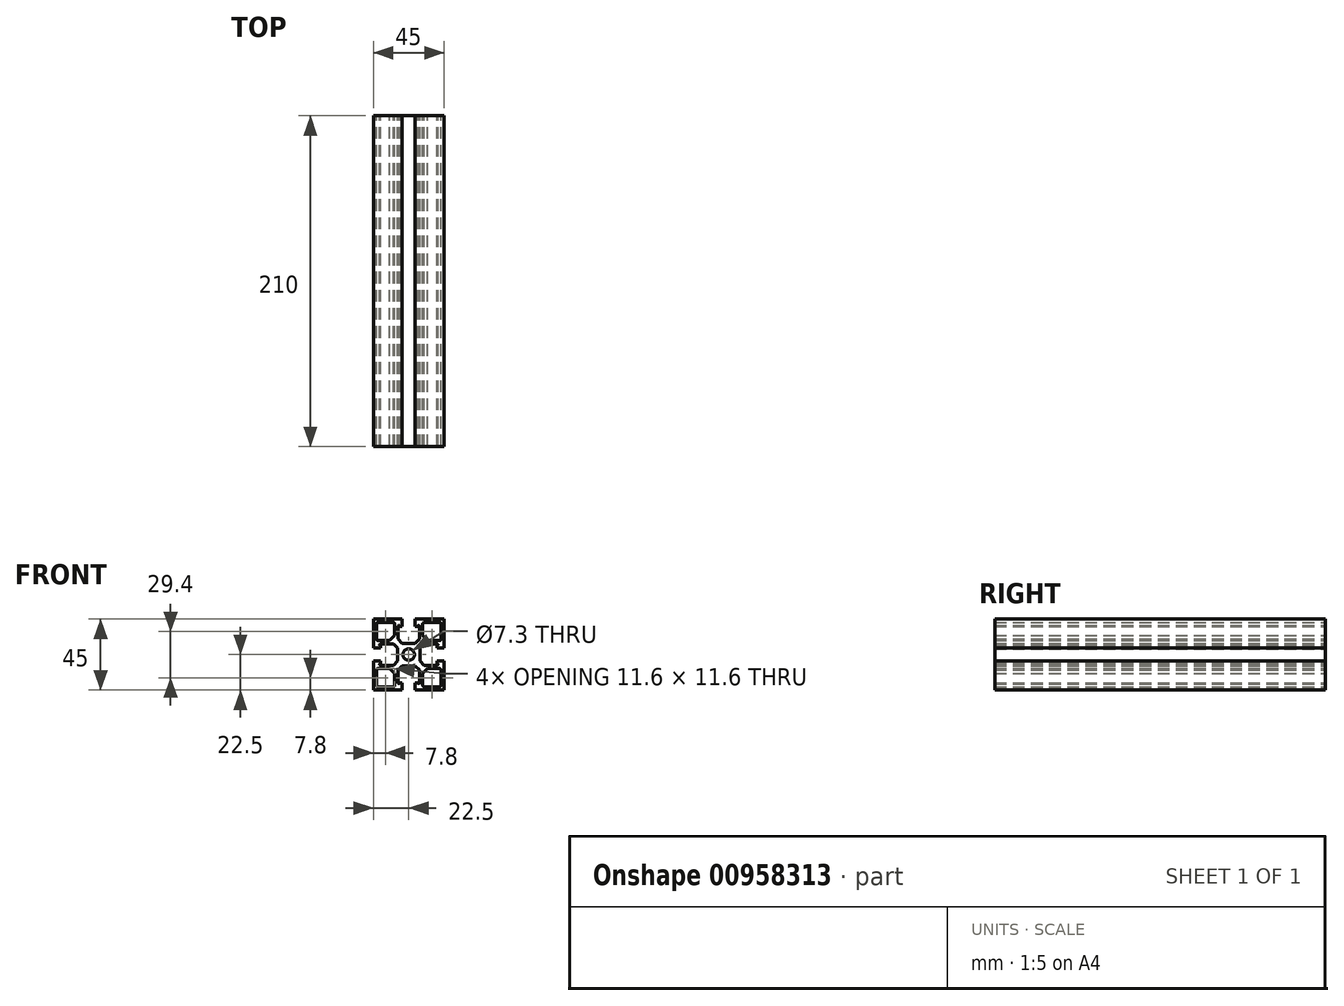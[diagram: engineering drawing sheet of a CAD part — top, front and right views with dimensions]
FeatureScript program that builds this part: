
annotation { "Feature Type Name" : "Feature", "Feature Type Description" : "" }
export const myFeature = defineFeature(function(context is Context, id is Id, definition is map)
    precondition{}
    {
        {
            var Q0;
            Q0=qCreatedBy(makeId("Front.planeOp"),FACE);
            var sketch = newSketch(context, id + "F0", { "sketchPlane" : qUnion([Q0])});
            skLineSegment(sketch, "E0", {"start": v(-22.5, 22.5) * mm, "end": v(-4.15, 22.5) * mm});
            skLineSegment(sketch, "E1", {"start": v(-4.15, 22.5) * mm, "end": v(-4.15, 18) * mm});
            skLineSegment(sketch, "E2", {"start": v(-4.15, 18) * mm, "end": v(-5.75, 18) * mm});
            skArc(sketch, "E3", {"start": v(-5.75, 18) * mm, "mid": v(-6.25, 18.5) * mm, "end": v(-6.75, 18) * mm});
            skLineSegment(sketch, "E4", {"start": v(-6.75, 18) * mm, "end": v(-6.75, 9.8) * mm});
            skLineSegment(sketch, "E5", {"start": v(-6.75, 9.8) * mm, "end": v(-4.15, 7.2) * mm});
            skLineSegment(sketch, "E6", {"start": v(-4.15, 7.2) * mm, "end": v(4.15, 7.2) * mm});
            skLineSegment(sketch, "E7", {"start": v(4.15, 7.2) * mm, "end": v(6.75, 9.8) * mm});
            skLineSegment(sketch, "E8", {"start": v(6.75, 9.8) * mm, "end": v(6.75, 18) * mm});
            skArc(sketch, "E9", {"start": v(6.75, 18) * mm, "mid": v(6.25, 18.5) * mm, "end": v(5.75, 18) * mm});
            skLineSegment(sketch, "E10", {"start": v(5.75, 18) * mm, "end": v(4.15, 18) * mm});
            skLineSegment(sketch, "E11", {"start": v(4.15, 18) * mm, "end": v(4.15, 22.5) * mm});
            skLineSegment(sketch, "E12", {"start": v(4.15, 22.5) * mm, "end": v(22.5, 22.5) * mm});
            skLineSegment(sketch, "E13", {"start": v(22.5, 22.5) * mm, "end": v(22.5, 4.15) * mm});
            skLineSegment(sketch, "E14", {"start": v(22.5, 4.15) * mm, "end": v(18, 4.15) * mm});
            skLineSegment(sketch, "E15", {"start": v(18, 4.15) * mm, "end": v(18, 5.75) * mm});
            skArc(sketch, "E16", {"start": v(18, 5.75) * mm, "mid": v(18.5, 6.25) * mm, "end": v(18, 6.75) * mm});
            skLineSegment(sketch, "E17", {"start": v(18, 6.75) * mm, "end": v(9.8, 6.75) * mm});
            skLineSegment(sketch, "E18", {"start": v(9.8, 6.75) * mm, "end": v(7.2, 4.15) * mm});
            skLineSegment(sketch, "E19", {"start": v(7.2, 4.15) * mm, "end": v(7.2, -4.15) * mm});
            skLineSegment(sketch, "E20", {"start": v(7.2, -4.15) * mm, "end": v(9.8, -6.75) * mm});
            skLineSegment(sketch, "E21", {"start": v(9.8, -6.75) * mm, "end": v(18, -6.75) * mm});
            skArc(sketch, "E22", {"start": v(18, -6.75) * mm, "mid": v(18.5, -6.25) * mm, "end": v(18, -5.75) * mm});
            skLineSegment(sketch, "E23", {"start": v(18, -5.75) * mm, "end": v(18, -4.15) * mm});
            skLineSegment(sketch, "E24", {"start": v(18, -4.15) * mm, "end": v(22.5, -4.15) * mm});
            skLineSegment(sketch, "E25", {"start": v(22.5, -4.15) * mm, "end": v(22.5, -22.5) * mm});
            skLineSegment(sketch, "E26", {"start": v(22.5, -22.5) * mm, "end": v(4.15, -22.5) * mm});
            skLineSegment(sketch, "E27", {"start": v(4.15, -22.5) * mm, "end": v(4.15, -18) * mm});
            skLineSegment(sketch, "E28", {"start": v(4.15, -18) * mm, "end": v(5.75, -18) * mm});
            skArc(sketch, "E29", {"start": v(5.75, -18) * mm, "mid": v(6.25, -18.5) * mm, "end": v(6.75, -18) * mm});
            skLineSegment(sketch, "E30", {"start": v(6.75, -18) * mm, "end": v(6.75, -9.8) * mm});
            skLineSegment(sketch, "E31", {"start": v(6.75, -9.8) * mm, "end": v(4.15, -7.2) * mm});
            skLineSegment(sketch, "E32", {"start": v(4.15, -7.2) * mm, "end": v(-4.15, -7.2) * mm});
            skLineSegment(sketch, "E33", {"start": v(-4.15, -7.2) * mm, "end": v(-6.75, -9.8) * mm});
            skLineSegment(sketch, "E34", {"start": v(-6.75, -9.8) * mm, "end": v(-6.75, -18) * mm});
            skArc(sketch, "E35", {"start": v(-6.75, -18) * mm, "mid": v(-6.25, -18.5) * mm, "end": v(-5.75, -18) * mm});
            skLineSegment(sketch, "E36", {"start": v(-5.75, -18) * mm, "end": v(-4.15, -18) * mm});
            skLineSegment(sketch, "E37", {"start": v(-4.15, -18) * mm, "end": v(-4.15, -22.5) * mm});
            skLineSegment(sketch, "E38", {"start": v(-4.15, -22.5) * mm, "end": v(-22.5, -22.5) * mm});
            skLineSegment(sketch, "E39", {"start": v(-22.5, -22.5) * mm, "end": v(-22.5, -4.15) * mm});
            skLineSegment(sketch, "E40", {"start": v(-22.5, -4.15) * mm, "end": v(-18, -4.15) * mm});
            skLineSegment(sketch, "E41", {"start": v(-18, -4.15) * mm, "end": v(-18, -5.75) * mm});
            skArc(sketch, "E42", {"start": v(-18, -5.75) * mm, "mid": v(-18.5, -6.25) * mm, "end": v(-18, -6.75) * mm});
            skLineSegment(sketch, "E43", {"start": v(-18, -6.75) * mm, "end": v(-9.8, -6.75) * mm});
            skLineSegment(sketch, "E44", {"start": v(-9.8, -6.75) * mm, "end": v(-7.2, -4.15) * mm});
            skLineSegment(sketch, "E45", {"start": v(-7.2, -4.15) * mm, "end": v(-7.2, 4.15) * mm});
            skLineSegment(sketch, "E46", {"start": v(-7.2, 4.15) * mm, "end": v(-9.8, 6.75) * mm});
            skLineSegment(sketch, "E47", {"start": v(-9.8, 6.75) * mm, "end": v(-18, 6.75) * mm});
            skArc(sketch, "E48", {"start": v(-18, 6.75) * mm, "mid": v(-18.5, 6.25) * mm, "end": v(-18, 5.75) * mm});
            skLineSegment(sketch, "E49", {"start": v(-18, 5.75) * mm, "end": v(-18, 4.15) * mm});
            skLineSegment(sketch, "E50", {"start": v(-18, 4.15) * mm, "end": v(-22.5, 4.15) * mm});
            skLineSegment(sketch, "E51", {"start": v(-22.5, 4.15) * mm, "end": v(-22.5, 22.5) * mm});
            skLineSegment(sketch, "E52", {"start": v(-19.5, 20.5) * mm, "end": v(-9.9, 20.5) * mm});
            skArc(sketch, "E53", {"start": v(-8.9, 19.5) * mm, "mid": v(-9.2, 20.2) * mm, "end": v(-9.9, 20.5) * mm});
            skLineSegment(sketch, "E54", {"start": v(-8.9, 19.5) * mm, "end": v(-8.9, 12.1) * mm});
            skLineSegment(sketch, "E55", {"start": v(-8.9, 12.1) * mm, "end": v(-12.1, 8.9) * mm});
            skLineSegment(sketch, "E56", {"start": v(-12.1, 8.9) * mm, "end": v(-19.5, 8.9) * mm});
            skArc(sketch, "E57", {"start": v(-20.5, 9.9) * mm, "mid": v(-20.2, 9.2) * mm, "end": v(-19.5, 8.9) * mm});
            skLineSegment(sketch, "E58", {"start": v(-20.5, 9.9) * mm, "end": v(-20.5, 19.5) * mm});
            skArc(sketch, "E59", {"start": v(-19.5, 20.5) * mm, "mid": v(-20.2, 20.2) * mm, "end": v(-20.5, 19.5) * mm});
            skLineSegment(sketch, "E60", {"start": v(8.9, 12.1) * mm, "end": v(8.9, 19.5) * mm});
            skArc(sketch, "E61", {"start": v(9.9, 20.5) * mm, "mid": v(9.2, 20.2) * mm, "end": v(8.9, 19.5) * mm});
            skLineSegment(sketch, "E62", {"start": v(9.9, 20.5) * mm, "end": v(19.5, 20.5) * mm});
            skArc(sketch, "E63", {"start": v(20.5, 19.5) * mm, "mid": v(20.2, 20.2) * mm, "end": v(19.5, 20.5) * mm});
            skLineSegment(sketch, "E64", {"start": v(20.5, 19.5) * mm, "end": v(20.5, 9.9) * mm});
            skLineSegment(sketch, "E65", {"start": v(19.5, 8.9) * mm, "end": v(12.1, 8.9) * mm});
            skLineSegment(sketch, "E66", {"start": v(12.1, 8.9) * mm, "end": v(8.9, 12.1) * mm});
            skArc(sketch, "E67", {"start": v(19.5, 8.9) * mm, "mid": v(20.2, 9.2) * mm, "end": v(20.5, 9.9) * mm});
            skLineSegment(sketch, "E68", {"start": v(12.1, -8.9) * mm, "end": v(8.9, -12.1) * mm});
            skLineSegment(sketch, "E69", {"start": v(8.9, -12.1) * mm, "end": v(8.9, -19.5) * mm});
            skArc(sketch, "E70", {"start": v(8.9, -19.5) * mm, "mid": v(9.2, -20.2) * mm, "end": v(9.9, -20.5) * mm});
            skLineSegment(sketch, "E71", {"start": v(9.9, -20.5) * mm, "end": v(19.5, -20.5) * mm});
            skLineSegment(sketch, "E72", {"start": v(20.5, -19.5) * mm, "end": v(20.5, -9.9) * mm});
            skArc(sketch, "E73", {"start": v(19.5, -20.5) * mm, "mid": v(20.2, -20.2) * mm, "end": v(20.5, -19.5) * mm});
            skArc(sketch, "E74", {"start": v(20.5, -9.9) * mm, "mid": v(20.2, -9.2) * mm, "end": v(19.5, -8.9) * mm});
            skLineSegment(sketch, "E75", {"start": v(12.1, -8.9) * mm, "end": v(19.5, -8.9) * mm});
            skLineSegment(sketch, "E76", {"start": v(-8.9, -19.5) * mm, "end": v(-8.9, -12.1) * mm});
            skLineSegment(sketch, "E77", {"start": v(-8.9, -12.1) * mm, "end": v(-12.1, -8.9) * mm});
            skLineSegment(sketch, "E78", {"start": v(-12.1, -8.9) * mm, "end": v(-19.5, -8.9) * mm});
            skLineSegment(sketch, "E79", {"start": v(-9.9, -20.5) * mm, "end": v(-19.5, -20.5) * mm});
            skLineSegment(sketch, "E80", {"start": v(-20.5, -19.5) * mm, "end": v(-20.5, -9.9) * mm});
            skArc(sketch, "E81", {"start": v(-19.5, -8.9) * mm, "mid": v(-20.2, -9.2) * mm, "end": v(-20.5, -9.9) * mm});
            skArc(sketch, "E82", {"start": v(-9.9, -20.5) * mm, "mid": v(-9.2, -20.2) * mm, "end": v(-8.9, -19.5) * mm});
            skArc(sketch, "E83", {"start": v(-20.5, -19.5) * mm, "mid": v(-20.2, -20.2) * mm, "end": v(-19.5, -20.5) * mm});
            skCircle(sketch, "E84", {"center": v(0, 0) * mm, "radius": 3.65 * mm});
            skSolve(sketch);
        }
        {
            var Q0;
            Q0=makeQuery(id+"F0.imprint","IMPRINT",FACE,{"disambiguationData":[TD([[makeQuery(id+"F0.imprint","IMPRINT",EDGE,{"derivedFrom":sQuery(id+"F0.wireOp",EDGE,"E0")}),-1.0]])]});
            extrude(context, id + "F1", {"entities" : qUnion([Q0]), "depth" : 210 * mm, "offsetDistance" : 25.4 * mm});
        }
    });
